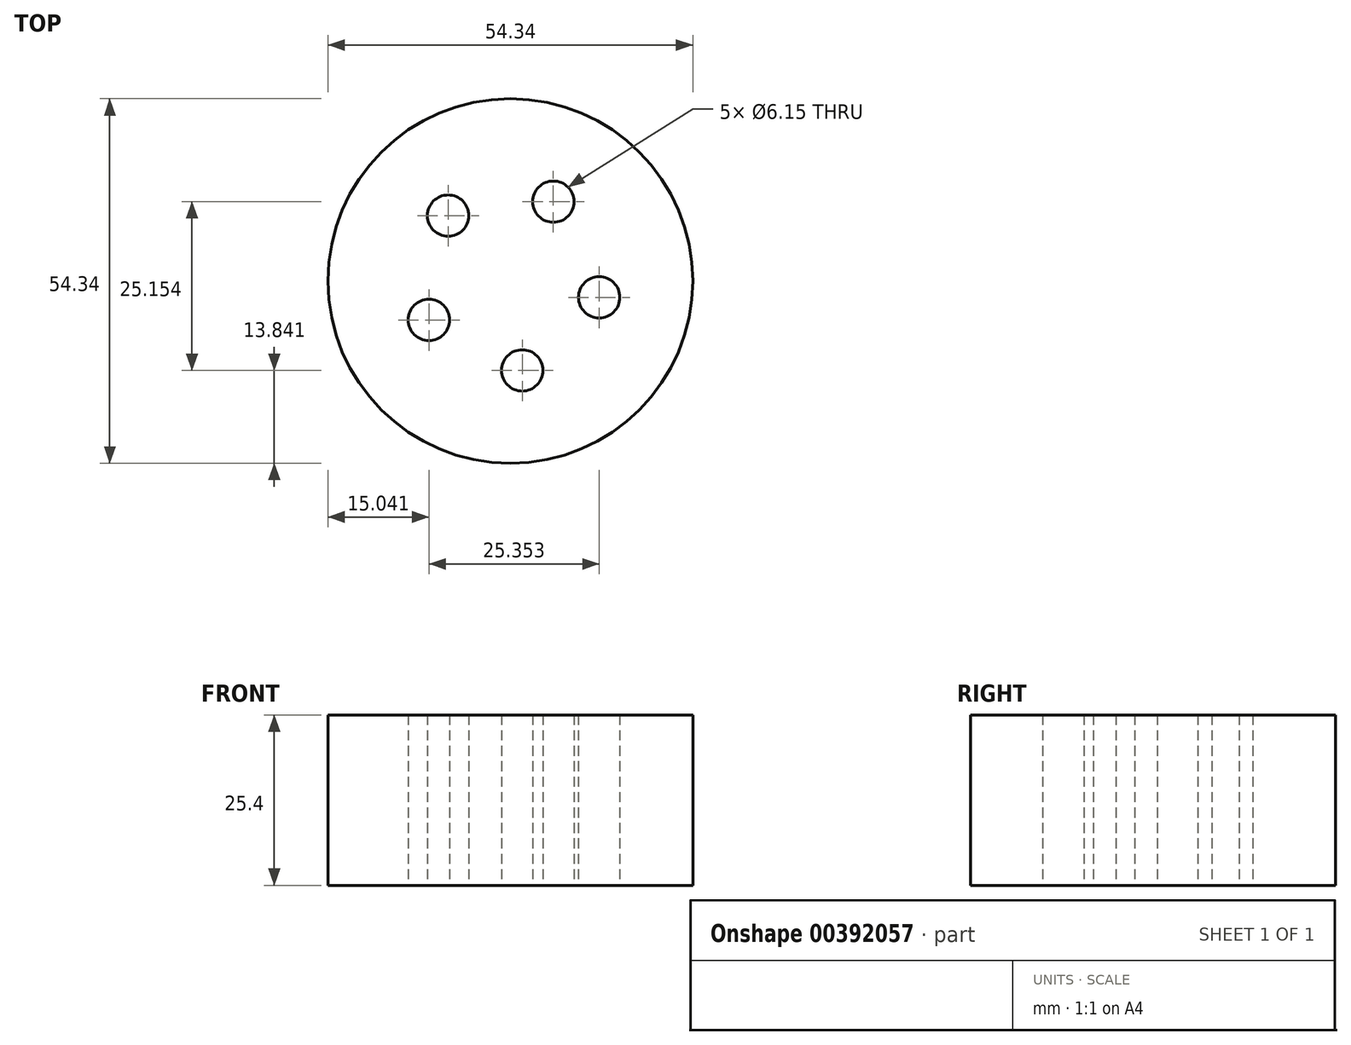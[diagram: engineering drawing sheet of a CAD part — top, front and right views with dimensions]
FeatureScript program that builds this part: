
annotation { "Feature Type Name" : "Feature", "Feature Type Description" : "" }
export const myFeature = defineFeature(function(context is Context, id is Id, definition is map)
    precondition{}
    {
        {
            var Q0;
            Q0=qCreatedBy(makeId("Top.planeOp"),FACE);
            var sketch = newSketch(context, id + "F0", { "sketchPlane" : qUnion([Q0])});
            skCircle(sketch, "E0", {"center": v(0, 0) * mm, "radius": 27.17 * mm});
            skCircle(sketch, "E1", {"center": v(13.22, -2.43) * mm, "radius": 3.08 * mm});
            skCircle(sketch, "E2.1.0", {"center": v(6.4, 11.82) * mm, "radius": 3.08 * mm});
            skCircle(sketch, "E2.2.0", {"center": v(-9.27, 9.74) * mm, "radius": 3.08 * mm});
            skCircle(sketch, "E2.3.0", {"center": v(-12.13, -5.8) * mm, "radius": 3.08 * mm});
            skCircle(sketch, "E2.4.0", {"center": v(1.77, -13.33) * mm, "radius": 3.08 * mm});
            skSolve(sketch);
        }
        {
            var Q0;
            Q0=makeQuery(id+"F0.imprint","IMPRINT",FACE,{"disambiguationData":[TD([[makeQuery(id+"F0.imprint","IMPRINT",EDGE,{"derivedFrom":sQuery(id+"F0.wireOp",EDGE,"E0")}),1.0]])]});
            extrude(context, id + "F1", {"entities" : qUnion([Q0]), "depth" : 25.4 * mm});
        }
    });
